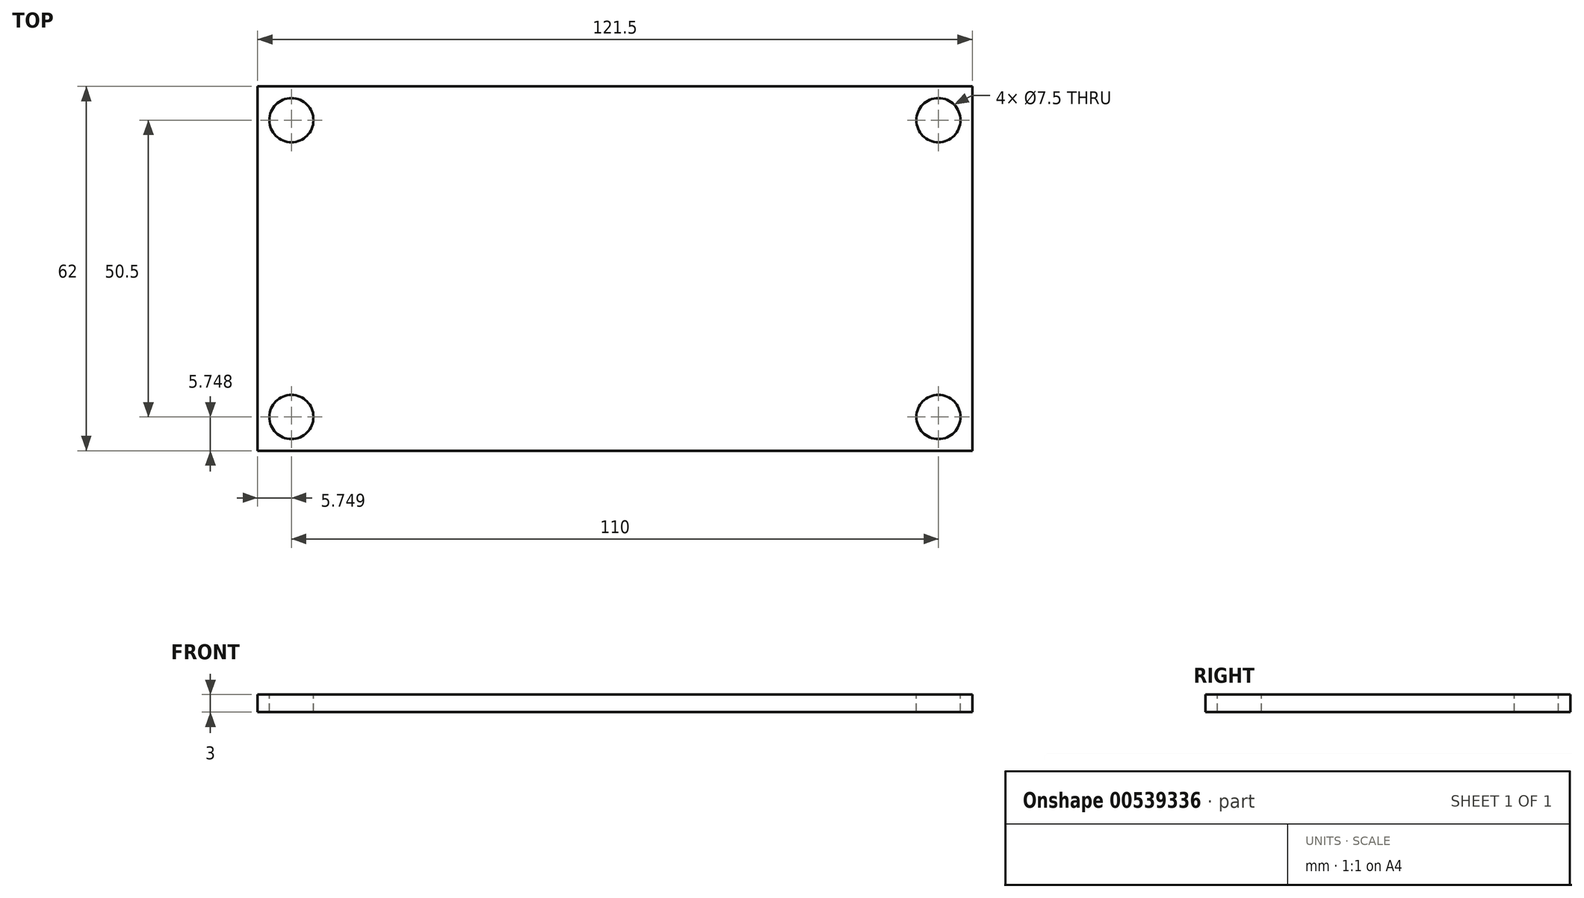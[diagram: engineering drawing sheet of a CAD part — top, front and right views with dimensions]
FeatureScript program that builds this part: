
annotation { "Feature Type Name" : "Feature", "Feature Type Description" : "" }
export const myFeature = defineFeature(function(context is Context, id is Id, definition is map)
    precondition{}
    {
        {
            var Q0;
            Q0=qCreatedBy(makeId("Top.planeOp"),FACE);
            var sketch = newSketch(context, id + "F0", { "sketchPlane" : qUnion([Q0])});
            skLineSegment(sketch, "E0.bottom", {"start": v(1558.5, -590.85) * mm, "end": v(1680, -590.85) * mm});
            skLineSegment(sketch, "E0.top", {"start": v(1558.5, -652.85) * mm, "end": v(1680, -652.85) * mm});
            skLineSegment(sketch, "E0.left", {"start": v(1558.5, -590.85) * mm, "end": v(1558.5, -652.85) * mm});
            skLineSegment(sketch, "E0.right", {"start": v(1680, -590.85) * mm, "end": v(1680, -652.85) * mm});
            skSolve(sketch);
        }
        {
            var Q0;
            Q0 = qSketchRegion(id + "F0", true);
            extrude(context, id + "F1", {"entities" : qUnion([Q0]), "depth" : 3 * mm, "offsetDistance" : 25.4 * mm});
        }
        {
            var Q0;
            Q0=makeQuery(id+"F1.opExtrude","CAP_FACE",FACE,{"disambiguationData":[OSD([sQuery(id+"F0.wireOp",EDGE,"E0.bottom"),sQuery(id+"F0.wireOp",EDGE,"E0.top"),sQuery(id+"F0.wireOp",EDGE,"E0.left"),sQuery(id+"F0.wireOp",EDGE,"E0.right")])],"isStart":false});
            var sketch = newSketch(context, id + "F2", { "sketchPlane" : qUnion([Q0])});
            skCircle(sketch, "E1", {"center": v(1564.26, -647.1) * mm, "radius": 2.3 * mm});
            skSolve(sketch);
        }
        {
            var Q0;
            Q0=sQuery(id+"F2.wireOp",VERTEX,"E1.center");
            var Q1;
            Q1=makeQuery(id+"F1.opExtrude","SWEPT_BODY",BODY,{"disambiguationData":[OSD([sQuery(id+"F0.wireOp",EDGE,"E0.bottom"),sQuery(id+"F0.wireOp",EDGE,"E0.top"),sQuery(id+"F0.wireOp",EDGE,"E0.left"),sQuery(id+"F0.wireOp",EDGE,"E0.right")])]});
            hole(context, id + "F3", {"style" : HoleStyle.SIMPLE, "endStyle" : HoleEndStyle.THROUGH, "holeDiameter" : 7.5 * mm, "isTappedThrough" : true, "tappedDepth" : 12 * mm, "tapClearance" : 3, "locations" : qUnion([Q0]), "scope" : qUnion([Q1])});
        }
        {
            var Q0;
            Q0=makeQuery(id+"F1.opExtrude","CAP_FACE",FACE,{"disambiguationData":[OSD([sQuery(id+"F0.wireOp",EDGE,"E0.bottom"),sQuery(id+"F0.wireOp",EDGE,"E0.top"),sQuery(id+"F0.wireOp",EDGE,"E0.left"),sQuery(id+"F0.wireOp",EDGE,"E0.right")])],"isStart":false});
            var sketch = newSketch(context, id + "F4", { "sketchPlane" : qUnion([Q0])});
            skCircle(sketch, "E2", {"center": v(1564.26, -596.6) * mm, "radius": 3.75 * mm});
            skSolve(sketch);
        }
        {
            var Q0;
            Q0=sQuery(id+"F4.wireOp",VERTEX,"E2.center");
            var Q1;
            Q1=makeQuery(id+"F1.opExtrude","SWEPT_BODY",BODY,{"disambiguationData":[OSD([sQuery(id+"F0.wireOp",EDGE,"E0.bottom"),sQuery(id+"F0.wireOp",EDGE,"E0.top"),sQuery(id+"F0.wireOp",EDGE,"E0.left"),sQuery(id+"F0.wireOp",EDGE,"E0.right")])]});
            hole(context, id + "F5", {"style" : HoleStyle.SIMPLE, "endStyle" : HoleEndStyle.THROUGH, "holeDiameter" : 7.5 * mm, "isTappedThrough" : true, "tappedDepth" : 12 * mm, "tapClearance" : 3, "locations" : qUnion([Q0]), "scope" : qUnion([Q1])});
        }
        {
            var Q0;
            Q0=makeQuery(id+"F1.opExtrude","CAP_FACE",FACE,{"disambiguationData":[OSD([sQuery(id+"F0.wireOp",EDGE,"E0.bottom"),sQuery(id+"F0.wireOp",EDGE,"E0.top"),sQuery(id+"F0.wireOp",EDGE,"E0.left"),sQuery(id+"F0.wireOp",EDGE,"E0.right")])],"isStart":false});
            var sketch = newSketch(context, id + "F6", { "sketchPlane" : qUnion([Q0])});
            skCircle(sketch, "E3", {"center": v(1674.26, -596.6) * mm, "radius": 3.75 * mm});
            skCircle(sketch, "E4", {"center": v(1674.26, -647.1) * mm, "radius": 3.75 * mm});
            skSolve(sketch);
        }
        {
            var Q0;
            Q0=sQuery(id+"F6.wireOp",VERTEX,"E3.center");
            var Q1;
            Q1=sQuery(id+"F6.wireOp",VERTEX,"E4.center");
            var Q2;
            Q2=makeQuery(id+"F1.opExtrude","SWEPT_BODY",BODY,{"disambiguationData":[OSD([sQuery(id+"F0.wireOp",EDGE,"E0.bottom"),sQuery(id+"F0.wireOp",EDGE,"E0.top"),sQuery(id+"F0.wireOp",EDGE,"E0.left"),sQuery(id+"F0.wireOp",EDGE,"E0.right")])]});
            hole(context, id + "F7", {"style" : HoleStyle.SIMPLE, "endStyle" : HoleEndStyle.THROUGH, "holeDiameter" : 7.5 * mm, "isTappedThrough" : true, "tappedDepth" : 12 * mm, "tapClearance" : 3, "locations" : qUnion([Q0, Q1]), "scope" : qUnion([Q2])});
        }
    });
